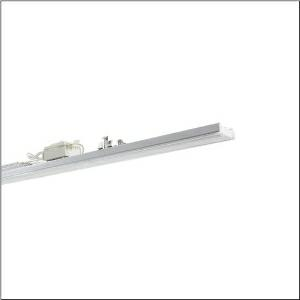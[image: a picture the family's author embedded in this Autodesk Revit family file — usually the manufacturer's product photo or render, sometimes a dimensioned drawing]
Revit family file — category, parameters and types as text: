
# Revit family: licross_11_recessed_mo_51tl14dn38xg
name_source: partatom
category: Lighting Fixtures
units: mm (PartAtom-declared; Revit-internal decimal feet)

## family parameters
Cut with Voids When Loaded = No
Host = Face
Light Source = No
Part Type = Normal
Room Calculation Point = No
Round Connector Dimension = Use Diameter
Shared = No

## types (1)
- --- (1 x LED, 8040 lm, 49.7 W, 3000K)
    Apparent Load = 50 VA
    CIE Flux Codes = 56 84 97 100 100
    Color Rendering = 80
    Color Temperature = 3000K
    Default Elevation = 1800 mm
    Description = Licross 11 Recessed MO, luminaire insert, of sheet steel, coil coated, white, length: 1.500mm, width: 66mm, height: 67mm, LED rated luminous flux: 8.040lm, light colour: 830, SDCM (Standard Deviation of Colour Matching)MacAdam ≤ 2 SDCM (initial), control gear: DALI 2, with plug, 5-pole, with phase selection, mains connection: 220..240V, AC, 50/60Hz, rated input power: 49.7W, internal wiring halogen-free, primary light control with lens, of plastic, primary optical cover: cover, of PMMA, light emission: direct distribution, primary light characteristic: asymmetric, protection rating (complete): IP40, insulation class (complete): insulation class I (protective earthing), certification: CE, ENEC, VDE, UKCA, protection symbol: D if used in an environment without relevant dust loads with corresponding accessories, impact resistance: IK06, permissible ambient temperature for indoor applications: -25..+35°C, corresponds to IFS (International Featured Standards) requirements for safety and quality in the food industry, reducing of maximum allowable ambient temperature of 5°C with ceiling mounting, LABS conformity tested according to VDMA 24364:2018-05, The light source and the operating device comply with the requirements of the Ecodesign Regulation (EU) 2019/2020 and are replaceable in accordance with this regulation, packaging unit: 1 piece
    Height = 58 mm
    Lamp = 1 x LED
    Lamp Light Flux = 8040 lm
    Lamp Power = 49.7 W
    Lamp count = 1
    Length = 1500 mm
    Luminous efficacy = 162 lm/W
    Manufacturer = Siteco
    ModVariant = No
    Model = 51TL14DN38XG
    Mounting Place = Ceiling
    Mounting Type = Pendant
    Number of Poles = 1
    OnlyDefault = Yes
    Power Factor = 1
    Product Name = Licross 11 Recessed MO
    Product group = luminaire insert | ceiling pendant
    ProductGroupID = 901
    Protection Class = Protection class I
    Protection Degree = IP 40
    RLX_Detail_Level = 1
    RLX_Emergency_Light_Flux = 0 lm
    RLX_Emergency_Type = 0
    RLX_Emergency_Type_DB = No
    RlxData = <blob elided: 25241 chars, md5=46c6ecd1>
    Socket = socket
    Standby Power = 0 W
    System Light Flux = 8040 lm
    System Power = 50 W
    Type Comments = factory setting: luminous flux: 100 % | dim-lin: 254 | 332 mA
    Type Image = l_1296930.jpg
    URL = http://relux.com
    VarID = @adj_038053
    Voltage = 0 V
    Weight = 0.00 kg
    Width = 66 mm

## geometry (parser evidence)
native form markers: Blend x4, Sweep x9
no freeform markers — native parametric forms only
